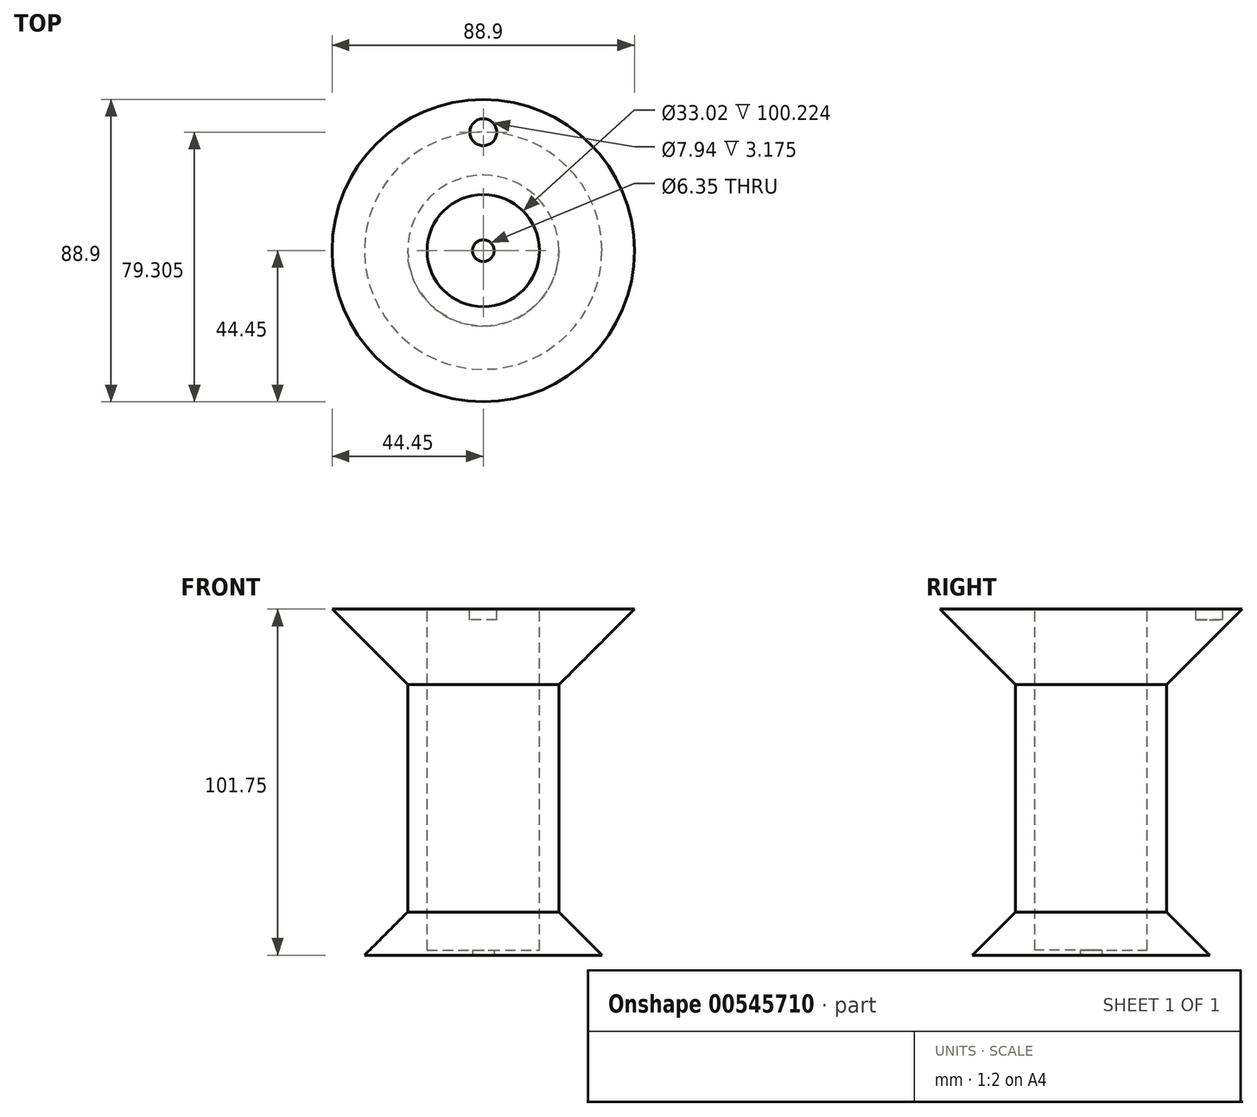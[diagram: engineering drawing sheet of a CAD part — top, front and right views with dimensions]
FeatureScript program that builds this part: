
annotation { "Feature Type Name" : "Feature", "Feature Type Description" : "" }
export const myFeature = defineFeature(function(context is Context, id is Id, definition is map)
    precondition{}
    {
        {
            var Q0;
            Q0=qCreatedBy(makeId("Top.planeOp"),FACE);
            var sketch = newSketch(context, id + "F0", { "sketchPlane" : qUnion([Q0])});
            skCircle(sketch, "E0", {"center": v(0, 0) * mm, "radius": 44.45 * mm});
            skCircle(sketch, "E1", {"center": v(0, 0) * mm, "radius": 16.51 * mm});
            skCircle(sketch, "E2", {"center": v(0, 0) * mm, "radius": 22.23 * mm});
            skSolve(sketch);
        }
        {
            var Q0;
            Q0=makeQuery(id+"F0.imprint","IMPRINT",FACE,{"disambiguationData":[TD([[makeQuery(id+"F0.imprint","IMPRINT",EDGE,{"derivedFrom":sQuery(id+"F0.wireOp",EDGE,"E1")}),-1.0]])]});
            extrude(context, id + "F1", {"entities" : qUnion([Q0]), "oppositeDirection" : true, "depth" : 76.2 * mm, "offsetDistance" : 25.4 * mm});
        }
        {
            var Q0;
            Q0=qCreatedBy(makeId("Top.planeOp"),FACE);
            var sketch = newSketch(context, id + "F2", { "sketchPlane" : qUnion([Q0])});
            skCircle(sketch, "E3", {"center": v(0, 0) * mm, "radius": 44.45 * mm});
            skSolve(sketch);
        }
        {
            var Q0;
            Q0=makeQuery(id+"F2.imprint","IMPRINT",FACE,{"disambiguationData":[TD([[makeQuery(id+"F2.imprint","IMPRINT",EDGE,{"derivedFrom":sQuery(id+"F2.wireOp",EDGE,"E3")}),1.0]])]});
            extrude(context, id + "F3", {"entities" : qUnion([Q0]), "operationType" : NewBodyOperationType.ADD, "depth" : 25.4 * mm, "offsetDistance" : 25.4 * mm});
        }
        {
            var Q0;
            Q0=makeQuery(id+"F3.opExtrude","CAP_FACE",FACE,{"disambiguationData":[OSD([sQuery(id+"F2.wireOp",EDGE,"E3")])],"isStart":false});
            var sketch = newSketch(context, id + "F4", { "sketchPlane" : qUnion([Q0])});
            skCircle(sketch, "E4", {"center": v(0, 34.86) * mm, "radius": 3.97 * mm});
            skSolve(sketch);
        }
        {
            var Q0;
            Q0 = qSketchRegion(id + "F4", true);
            extrude(context, id + "F5", {"entities" : qUnion([Q0]), "operationType" : NewBodyOperationType.REMOVE, "oppositeDirection" : true, "depth" : 3.17 * mm, "offsetDistance" : 25.4 * mm});
        }
        {
            var Q0;
            Q0=makeQuery(id+"F3.opExtrude","CAP_FACE",FACE,{"disambiguationData":[OSD([sQuery(id+"F2.wireOp",EDGE,"E3")])],"isStart":false});
            var sketch = newSketch(context, id + "F6", { "sketchPlane" : qUnion([Q0])});
            skCircle(sketch, "E5", {"center": v(0, 0) * mm, "radius": 16.51 * mm});
            skSolve(sketch);
        }
        {
            var Q0;
            Q0 = qSketchRegion(id + "F6", true);
            extrude(context, id + "F7", {"entities" : qUnion([Q0]), "operationType" : NewBodyOperationType.REMOVE, "oppositeDirection" : true, "depth" : 25.4 * mm, "offsetDistance" : 25.4 * mm});
        }
        {
            var Q0;
            Q0=makeQuery(id+"F3.opExtrude","CAP_EDGE",EDGE,{"disambiguationData":[OSD([sQuery(id+"F2.wireOp",EDGE,"E3")])],"isStart":true});
            chamfer(context, id + "F8", {"entities" : qUnion([Q0]), "width" : 25.4 * mm, "tangentPropagation" : true});
        }
        {
            var Q0;
            Q0=qCreatedBy(makeId("Front.planeOp"),FACE);
            var sketch = newSketch(context, id + "F9", { "sketchPlane" : qUnion([Q0])});
            skLineSegment(sketch, "E6", {"start": v(-22.22, -76.35) * mm, "end": v(-22.22, -63.65) * mm});
            skLineSegment(sketch, "E7", {"start": v(-22.22, -76.35) * mm, "end": v(-34.9, -76.35) * mm});
            skLineSegment(sketch, "E8", {"start": v(-34.9, -76.35) * mm, "end": v(-22.22, -63.65) * mm});
            skSolve(sketch);
        }
        {
            var Q0;
            Q0 = qSketchRegion(id + "F9", true);
            var Q1;
            Q1=makeQuery(id+"F1.opExtrude","CAP_EDGE",EDGE,{"disambiguationData":[OSD([sQuery(id+"F0.wireOp",EDGE,"E2")])],"isStart":false});
            revolve(context, id + "F10", {"operationType" : NewBodyOperationType.ADD, "entities" : qUnion([Q0]), "axis" : qUnion([Q1]), "revolveType" : RevolveType.FULL});
        }
        {
            var Q0;
            Q0=makeQuery(id+"F10.opRevolve","SWEPT_FACE",FACE,{"disambiguationData":[OSD([sQuery(id+"F9.wireOp",EDGE,"E7")])]});
            var sketch = newSketch(context, id + "F11", { "sketchPlane" : qUnion([Q0])});
            skCircle(sketch, "E9", {"center": v(0, 0) * mm, "radius": 24.28 * mm});
            skSolve(sketch);
        }
        {
            var Q0;
            Q0 = qSketchRegion(id + "F11", true);
            extrude(context, id + "F12", {"entities" : qUnion([Q0]), "operationType" : NewBodyOperationType.ADD, "oppositeDirection" : true, "depth" : 1.52 * mm, "offsetDistance" : 25.4 * mm});
        }
        {
            var Q0;
            Q0=makeQuery(id+"F12.boolean.opBoolean","MERGE",FACE,{"derivedFrom":[makeQuery(id+"F10.opRevolve","SWEPT_FACE",FACE,{"disambiguationData":[OSD([sQuery(id+"F9.wireOp",EDGE,"E7")])]}),makeQuery(id+"F12.opExtrude","CAP_FACE",FACE,{"disambiguationData":[OSD([sQuery(id+"F11.wireOp",EDGE,"E9")])],"isStart":true})]});
            var sketch = newSketch(context, id + "F13", { "sketchPlane" : qUnion([Q0])});
            skCircle(sketch, "E10", {"center": v(0, 0) * mm, "radius": 3.18 * mm});
            skSolve(sketch);
        }
        {
            var Q0;
            Q0=makeQuery(id+"F13.imprint","IMPRINT",FACE,{"disambiguationData":[TD([[makeQuery(id+"F13.imprint","IMPRINT",EDGE,{"derivedFrom":sQuery(id+"F13.wireOp",EDGE,"E10")}),1.0]])]});
            extrude(context, id + "F14", {"entities" : qUnion([Q0]), "operationType" : NewBodyOperationType.REMOVE, "oppositeDirection" : true, "depth" : 25.4 * mm, "offsetDistance" : 25.4 * mm});
        }
    });
